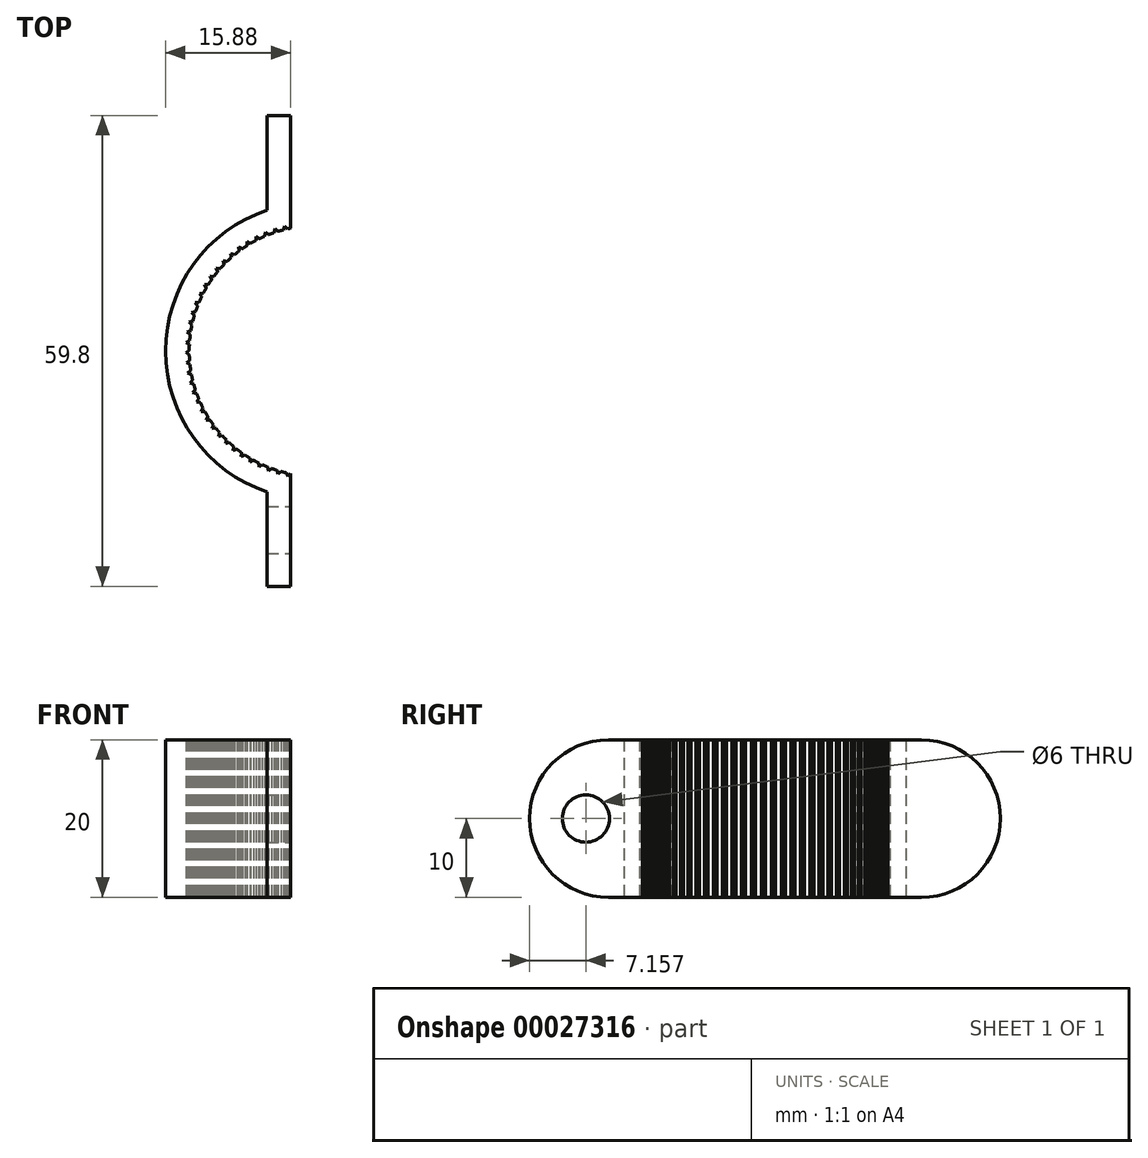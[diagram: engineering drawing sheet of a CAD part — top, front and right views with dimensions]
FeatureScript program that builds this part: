
annotation { "Feature Type Name" : "Feature", "Feature Type Description" : "" }
export const myFeature = defineFeature(function(context is Context, id is Id, definition is map)
    precondition{}
    {
        {
            var Q0;
            Q0=qCreatedBy(makeId("Top.planeOp"),FACE);
            var sketch = newSketch(context, id + "F0", { "sketchPlane" : qUnion([Q0])});
            skLineSegment(sketch, "E0", {"start": v(0, -18.88) * mm, "end": v(0, 18.88) * mm, "construction": true});
            skCircle(sketch, "E1", {"center": v(0, 0) * mm, "radius": 15.88 * mm});
            skCircle(sketch, "E2", {"center": v(0, 0) * mm, "radius": 18.88 * mm});
            skLineSegment(sketch, "E3", {"start": v(-3, 15.59) * mm, "end": v(-3, 29.9) * mm});
            skLineSegment(sketch, "E4", {"start": v(-3, 29.9) * mm, "end": v(-6, 29.9) * mm});
            skLineSegment(sketch, "E5", {"start": v(-6, 29.9) * mm, "end": v(-6, 17.9) * mm});
            skLineSegment(sketch, "E6", {"start": v(-15.88, 0) * mm, "end": v(15.88, 0) * mm, "construction": true});
            skLineSegment(sketch, "E7.MirrorCS", {"start": v(-6, -29.9) * mm, "end": v(-6, -17.9) * mm});
            skLineSegment(sketch, "E8.MirrorCS", {"start": v(-3, -29.9) * mm, "end": v(-6, -29.9) * mm});
            skLineSegment(sketch, "E9.MirrorCS", {"start": v(-3, -15.59) * mm, "end": v(-3, -29.9) * mm});
            skLineSegment(sketch, "E10", {"start": v(-15.88, 0) * mm, "end": v(-18.88, 0) * mm, "construction": true});
            skLineSegment(sketch, "E11", {"start": v(-3, -15.59) * mm, "end": v(-3.34, -15.96) * mm});
            skLineSegment(sketch, "E12", {"start": v(-3.34, -15.96) * mm, "end": v(-3.5, -15.48) * mm});
            skLineSegment(sketch, "E13.1.0", {"start": v(-4.23, -15.3) * mm, "end": v(-4.6, -15.64) * mm});
            skLineSegment(sketch, "E13.1.1", {"start": v(-4.6, -15.64) * mm, "end": v(-4.72, -15.16) * mm});
            skLineSegment(sketch, "E13.2.0", {"start": v(-5.43, -14.92) * mm, "end": v(-5.82, -15.23) * mm});
            skLineSegment(sketch, "E13.2.1", {"start": v(-5.82, -15.23) * mm, "end": v(-5.9, -14.73) * mm});
            skLineSegment(sketch, "E13.3.0", {"start": v(-6.6, -14.44) * mm, "end": v(-7.01, -14.72) * mm});
            skLineSegment(sketch, "E13.3.1", {"start": v(-7.01, -14.72) * mm, "end": v(-7.06, -14.22) * mm});
            skLineSegment(sketch, "E13.4.0", {"start": v(-7.73, -13.87) * mm, "end": v(-8.16, -14.11) * mm});
            skLineSegment(sketch, "E13.4.1", {"start": v(-8.16, -14.11) * mm, "end": v(-8.17, -13.61) * mm});
            skLineSegment(sketch, "E13.5.0", {"start": v(-8.8, -13.21) * mm, "end": v(-9.26, -13.42) * mm});
            skLineSegment(sketch, "E13.5.1", {"start": v(-9.26, -13.42) * mm, "end": v(-9.22, -12.92) * mm});
            skLineSegment(sketch, "E13.6.0", {"start": v(-9.82, -12.47) * mm, "end": v(-10.3, -12.64) * mm});
            skLineSegment(sketch, "E13.6.1", {"start": v(-10.3, -12.64) * mm, "end": v(-10.22, -12.15) * mm});
            skLineSegment(sketch, "E13.7.0", {"start": v(-10.78, -11.65) * mm, "end": v(-11.27, -11.78) * mm});
            skLineSegment(sketch, "E13.7.1", {"start": v(-11.27, -11.78) * mm, "end": v(-11.15, -11.3) * mm});
            skLineSegment(sketch, "E13.8.0", {"start": v(-11.68, -10.76) * mm, "end": v(-12.17, -10.85) * mm});
            skLineSegment(sketch, "E13.8.1", {"start": v(-12.17, -10.85) * mm, "end": v(-12.02, -10.37) * mm});
            skLineSegment(sketch, "E13.9.0", {"start": v(-12.5, -9.8) * mm, "end": v(-13, -9.85) * mm});
            skLineSegment(sketch, "E13.9.1", {"start": v(-13, -9.85) * mm, "end": v(-12.8, -9.39) * mm});
            skLineSegment(sketch, "E13.10.0", {"start": v(-13.23, -8.77) * mm, "end": v(-13.73, -8.79) * mm});
            skLineSegment(sketch, "E13.10.1", {"start": v(-13.73, -8.79) * mm, "end": v(-13.5, -8.34) * mm});
            skLineSegment(sketch, "E13.11.0", {"start": v(-13.89, -7.7) * mm, "end": v(-14.39, -7.67) * mm});
            skLineSegment(sketch, "E13.11.1", {"start": v(-14.39, -7.67) * mm, "end": v(-14.13, -7.24) * mm});
            skLineSegment(sketch, "E13.12.0", {"start": v(-14.45, -6.56) * mm, "end": v(-14.95, -6.5) * mm});
            skLineSegment(sketch, "E13.12.1", {"start": v(-14.95, -6.5) * mm, "end": v(-14.66, -6.1) * mm});
            skLineSegment(sketch, "E13.13.0", {"start": v(-14.93, -5.4) * mm, "end": v(-15.42, -5.3) * mm});
            skLineSegment(sketch, "E13.13.1", {"start": v(-15.42, -5.3) * mm, "end": v(-15.1, -4.91) * mm});
            skLineSegment(sketch, "E13.14.0", {"start": v(-15.31, -4.2) * mm, "end": v(-15.8, -4.05) * mm});
            skLineSegment(sketch, "E13.14.1", {"start": v(-15.8, -4.05) * mm, "end": v(-15.44, -3.7) * mm});
            skLineSegment(sketch, "E13.15.0", {"start": v(-15.6, -2.96) * mm, "end": v(-16.06, -2.78) * mm});
            skLineSegment(sketch, "E13.15.1", {"start": v(-16.06, -2.78) * mm, "end": v(-15.68, -2.46) * mm});
            skLineSegment(sketch, "E13.16.0", {"start": v(-15.78, -1.71) * mm, "end": v(-16.23, -1.5) * mm});
            skLineSegment(sketch, "E13.16.1", {"start": v(-16.23, -1.5) * mm, "end": v(-15.83, -1.2) * mm});
            skLineSegment(sketch, "E13.17.0", {"start": v(-15.87, -0.45) * mm, "end": v(-16.3, -0.2) * mm});
            skLineSegment(sketch, "E13.17.1", {"start": v(-16.3, -0.2) * mm, "end": v(-15.87, 0.06) * mm});
            skLineSegment(sketch, "E13.18.0", {"start": v(-15.85, 0.8) * mm, "end": v(-16.27, 1.1) * mm});
            skLineSegment(sketch, "E13.18.1", {"start": v(-16.27, 1.1) * mm, "end": v(-15.82, 1.32) * mm});
            skLineSegment(sketch, "E13.19.0", {"start": v(-15.74, 2.07) * mm, "end": v(-16.13, 2.38) * mm});
            skLineSegment(sketch, "E13.19.1", {"start": v(-16.13, 2.38) * mm, "end": v(-15.67, 2.57) * mm});
            skLineSegment(sketch, "E13.20.0", {"start": v(-15.53, 3.3) * mm, "end": v(-15.89, 3.65) * mm});
            skLineSegment(sketch, "E13.20.1", {"start": v(-15.89, 3.65) * mm, "end": v(-15.41, 3.8) * mm});
            skLineSegment(sketch, "E13.21.0", {"start": v(-15.21, 4.53) * mm, "end": v(-15.55, 4.9) * mm});
            skLineSegment(sketch, "E13.21.1", {"start": v(-15.55, 4.9) * mm, "end": v(-15.06, 5.02) * mm});
            skLineSegment(sketch, "E13.22.0", {"start": v(-14.8, 5.73) * mm, "end": v(-15.1, 6.13) * mm});
            skLineSegment(sketch, "E13.22.1", {"start": v(-15.1, 6.13) * mm, "end": v(-14.61, 6.2) * mm});
            skLineSegment(sketch, "E13.23.0", {"start": v(-14.3, 6.89) * mm, "end": v(-14.57, 7.3) * mm});
            skLineSegment(sketch, "E13.23.1", {"start": v(-14.57, 7.3) * mm, "end": v(-14.08, 7.34) * mm});
            skLineSegment(sketch, "E13.24.0", {"start": v(-13.71, 8) * mm, "end": v(-13.95, 8.44) * mm});
            skLineSegment(sketch, "E13.24.1", {"start": v(-13.95, 8.44) * mm, "end": v(-13.45, 8.44) * mm});
            skLineSegment(sketch, "E13.25.0", {"start": v(-13.03, 9.06) * mm, "end": v(-13.23, 9.52) * mm});
            skLineSegment(sketch, "E13.25.1", {"start": v(-13.23, 9.52) * mm, "end": v(-12.73, 9.48) * mm});
            skLineSegment(sketch, "E13.26.0", {"start": v(-12.27, 10.07) * mm, "end": v(-12.43, 10.54) * mm});
            skLineSegment(sketch, "E13.26.1", {"start": v(-12.43, 10.54) * mm, "end": v(-11.94, 10.46) * mm});
            skLineSegment(sketch, "E13.27.0", {"start": v(-11.43, 11.01) * mm, "end": v(-11.56, 11.5) * mm});
            skLineSegment(sketch, "E13.27.1", {"start": v(-11.56, 11.5) * mm, "end": v(-11.07, 11.38) * mm});
            skLineSegment(sketch, "E13.28.0", {"start": v(-10.52, 11.89) * mm, "end": v(-10.6, 12.38) * mm});
            skLineSegment(sketch, "E13.28.1", {"start": v(-10.6, 12.38) * mm, "end": v(-10.13, 12.22) * mm});
            skLineSegment(sketch, "E13.29.0", {"start": v(-9.54, 12.69) * mm, "end": v(-9.6, 13.18) * mm});
            skLineSegment(sketch, "E13.29.1", {"start": v(-9.6, 13.18) * mm, "end": v(-9.13, 12.99) * mm});
            skLineSegment(sketch, "E13.30.0", {"start": v(-8.5, 13.4) * mm, "end": v(-8.51, 13.9) * mm});
            skLineSegment(sketch, "E13.30.1", {"start": v(-8.51, 13.9) * mm, "end": v(-8.07, 13.67) * mm});
            skLineSegment(sketch, "E13.31.0", {"start": v(-7.41, 14.04) * mm, "end": v(-7.38, 14.54) * mm});
            skLineSegment(sketch, "E13.31.1", {"start": v(-7.38, 14.54) * mm, "end": v(-6.96, 14.27) * mm});
            skLineSegment(sketch, "E13.32.0", {"start": v(-6.28, 14.58) * mm, "end": v(-6.2, 15.08) * mm});
            skLineSegment(sketch, "E13.32.1", {"start": v(-6.2, 15.08) * mm, "end": v(-5.8, 14.78) * mm});
            skLineSegment(sketch, "E13.33.0", {"start": v(-5.1, 15.03) * mm, "end": v(-4.99, 15.52) * mm});
            skLineSegment(sketch, "E13.33.1", {"start": v(-4.99, 15.52) * mm, "end": v(-4.61, 15.2) * mm});
            skLineSegment(sketch, "E13.34.0", {"start": v(-3.89, 15.4) * mm, "end": v(-3.74, 15.87) * mm});
            skLineSegment(sketch, "E13.34.1", {"start": v(-3.74, 15.87) * mm, "end": v(-3.39, 15.5) * mm});
            skLineSegment(sketch, "E13.35.0", {"start": v(-2.65, 15.65) * mm, "end": v(-2.46, 16.12) * mm});
            skLineSegment(sketch, "E13.35.1", {"start": v(-2.46, 16.12) * mm, "end": v(-2.15, 15.73) * mm});
            skLineSegment(sketch, "E13.36.0", {"start": v(-1.4, 15.81) * mm, "end": v(-1.18, 16.26) * mm});
            skLineSegment(sketch, "E13.36.1", {"start": v(-1.18, 16.26) * mm, "end": v(-0.89, 15.85) * mm});
            skLineSegment(sketch, "E13.37.0", {"start": v(-0.14, 15.87) * mm, "end": v(0.12, 16.3) * mm});
            skLineSegment(sketch, "E13.37.1", {"start": v(0.12, 16.3) * mm, "end": v(0.37, 15.87) * mm});
            skLineSegment(sketch, "E13.38.0", {"start": v(1.12, 15.84) * mm, "end": v(1.42, 16.24) * mm});
            skLineSegment(sketch, "E13.38.1", {"start": v(1.42, 16.24) * mm, "end": v(1.63, 15.8) * mm});
            skLineSegment(sketch, "E13.39.0", {"start": v(2.38, 15.7) * mm, "end": v(2.7, 16.08) * mm});
            skLineSegment(sketch, "E13.39.1", {"start": v(2.7, 16.08) * mm, "end": v(2.88, 15.61) * mm});
            skLineSegment(sketch, "E13.anchor1", {"start": v(0, 0) * mm, "end": v(-3.34, -15.96) * mm, "construction": true});
            skLineSegment(sketch, "E13.anchor2", {"start": v(0, 0) * mm, "end": v(-3.34, -15.96) * mm, "construction": true});
            skLineSegment(sketch, "E14.2.40.0", {"start": v(3.62, 15.46) * mm, "end": v(3.97, 15.81) * mm});
            skLineSegment(sketch, "E14.3.40.0", {"start": v(3.97, 15.81) * mm, "end": v(4.11, 15.33) * mm});
            skLineSegment(sketch, "E14.2.41.0", {"start": v(4.83, 15.12) * mm, "end": v(5.21, 15.45) * mm});
            skLineSegment(sketch, "E14.3.41.0", {"start": v(5.21, 15.45) * mm, "end": v(5.32, 14.96) * mm});
            skLineSegment(sketch, "E14.2.42.0", {"start": v(6.02, 14.69) * mm, "end": v(6.42, 14.98) * mm});
            skLineSegment(sketch, "E14.3.42.0", {"start": v(6.42, 14.98) * mm, "end": v(6.49, 14.49) * mm});
            skLineSegment(sketch, "E14.2.43.0", {"start": v(7.17, 14.16) * mm, "end": v(7.6, 14.43) * mm});
            skLineSegment(sketch, "E14.3.43.0", {"start": v(7.6, 14.43) * mm, "end": v(7.62, 13.93) * mm});
            skLineSegment(sketch, "E14.2.44.0", {"start": v(8.27, 13.55) * mm, "end": v(8.72, 13.78) * mm});
            skLineSegment(sketch, "E14.3.44.0", {"start": v(8.72, 13.78) * mm, "end": v(8.7, 13.28) * mm});
            skLineSegment(sketch, "E14.2.45.0", {"start": v(9.32, 12.85) * mm, "end": v(9.78, 13.04) * mm});
            skLineSegment(sketch, "E14.3.45.0", {"start": v(9.78, 13.04) * mm, "end": v(9.73, 12.54) * mm});
            skLineSegment(sketch, "E14.2.46.0", {"start": v(10.31, 12.07) * mm, "end": v(10.79, 12.22) * mm});
            skLineSegment(sketch, "E14.3.46.0", {"start": v(10.79, 12.22) * mm, "end": v(10.7, 11.73) * mm});
            skLineSegment(sketch, "E14.2.47.0", {"start": v(11.24, 11.21) * mm, "end": v(11.73, 11.33) * mm});
            skLineSegment(sketch, "E14.3.47.0", {"start": v(11.73, 11.33) * mm, "end": v(11.6, 10.84) * mm});
            skLineSegment(sketch, "E14.2.48.0", {"start": v(12.1, 10.28) * mm, "end": v(12.59, 10.36) * mm});
            skLineSegment(sketch, "E14.3.48.0", {"start": v(12.59, 10.36) * mm, "end": v(12.42, 9.89) * mm});
            skLineSegment(sketch, "E14.2.49.0", {"start": v(12.87, 9.29) * mm, "end": v(13.37, 9.33) * mm});
            skLineSegment(sketch, "E14.3.49.0", {"start": v(13.37, 9.33) * mm, "end": v(13.17, 8.87) * mm});
            skLineSegment(sketch, "E14.2.50.0", {"start": v(13.57, 8.24) * mm, "end": v(14.07, 8.23) * mm});
            skLineSegment(sketch, "E14.3.50.0", {"start": v(14.07, 8.23) * mm, "end": v(13.83, 7.8) * mm});
            skLineSegment(sketch, "E14.2.51.0", {"start": v(14.18, 7.13) * mm, "end": v(14.68, 7.1) * mm});
            skLineSegment(sketch, "E14.3.51.0", {"start": v(14.68, 7.1) * mm, "end": v(14.4, 6.67) * mm});
            skLineSegment(sketch, "E14.2.52.0", {"start": v(14.7, 5.98) * mm, "end": v(15.2, 5.9) * mm});
            skLineSegment(sketch, "E14.3.52.0", {"start": v(15.2, 5.9) * mm, "end": v(14.89, 5.5) * mm});
            skLineSegment(sketch, "E14.2.53.0", {"start": v(15.13, 4.8) * mm, "end": v(15.62, 4.68) * mm});
            skLineSegment(sketch, "E14.3.53.0", {"start": v(15.62, 4.68) * mm, "end": v(15.28, 4.3) * mm});
            skLineSegment(sketch, "E14.2.54.0", {"start": v(15.47, 3.58) * mm, "end": v(15.94, 3.42) * mm});
            skLineSegment(sketch, "E14.3.54.0", {"start": v(15.94, 3.42) * mm, "end": v(15.57, 3.08) * mm});
            skLineSegment(sketch, "E14.2.55.0", {"start": v(15.7, 2.34) * mm, "end": v(16.16, 2.14) * mm});
            skLineSegment(sketch, "E14.3.55.0", {"start": v(16.16, 2.14) * mm, "end": v(15.77, 1.83) * mm});
            skLineSegment(sketch, "E14.2.56.0", {"start": v(15.84, 1.08) * mm, "end": v(16.28, 0.85) * mm});
            skLineSegment(sketch, "E14.3.56.0", {"start": v(16.28, 0.85) * mm, "end": v(15.86, 0.57) * mm});
            skLineSegment(sketch, "E14.2.57.0", {"start": v(15.87, -0.18) * mm, "end": v(16.3, -0.44) * mm});
            skLineSegment(sketch, "E14.3.57.0", {"start": v(16.3, -0.44) * mm, "end": v(15.86, -0.69) * mm});
            skLineSegment(sketch, "E14.2.58.0", {"start": v(15.8, -1.44) * mm, "end": v(16.2, -1.74) * mm});
            skLineSegment(sketch, "E14.3.58.0", {"start": v(16.2, -1.74) * mm, "end": v(15.76, -1.95) * mm});
            skLineSegment(sketch, "E14.2.59.0", {"start": v(15.65, -2.69) * mm, "end": v(16.02, -3.02) * mm});
            skLineSegment(sketch, "E14.3.59.0", {"start": v(16.02, -3.02) * mm, "end": v(15.55, -3.2) * mm});
            skLineSegment(sketch, "E14.2.60.0", {"start": v(15.38, -3.92) * mm, "end": v(15.73, -4.28) * mm});
            skLineSegment(sketch, "E14.3.60.0", {"start": v(15.73, -4.28) * mm, "end": v(15.25, -4.42) * mm});
            skLineSegment(sketch, "E14.2.61.0", {"start": v(15.02, -5.13) * mm, "end": v(15.34, -5.52) * mm});
            skLineSegment(sketch, "E14.3.61.0", {"start": v(15.34, -5.52) * mm, "end": v(14.85, -5.61) * mm});
            skLineSegment(sketch, "E14.2.62.0", {"start": v(14.57, -6.31) * mm, "end": v(14.85, -6.72) * mm});
            skLineSegment(sketch, "E14.3.62.0", {"start": v(14.85, -6.72) * mm, "end": v(14.36, -6.78) * mm});
            skLineSegment(sketch, "E14.2.63.0", {"start": v(14.02, -7.45) * mm, "end": v(14.27, -7.88) * mm});
            skLineSegment(sketch, "E14.3.63.0", {"start": v(14.27, -7.88) * mm, "end": v(13.77, -7.9) * mm});
            skLineSegment(sketch, "E14.2.64.0", {"start": v(13.38, -8.54) * mm, "end": v(13.6, -8.99) * mm});
            skLineSegment(sketch, "E14.3.64.0", {"start": v(13.6, -8.99) * mm, "end": v(13.1, -8.96) * mm});
            skLineSegment(sketch, "E14.2.65.0", {"start": v(12.66, -9.57) * mm, "end": v(12.84, -10.04) * mm});
            skLineSegment(sketch, "E14.3.65.0", {"start": v(12.84, -10.04) * mm, "end": v(12.35, -9.98) * mm});
            skLineSegment(sketch, "E14.2.66.0", {"start": v(11.86, -10.55) * mm, "end": v(12, -11.03) * mm});
            skLineSegment(sketch, "E14.3.66.0", {"start": v(12, -11.03) * mm, "end": v(11.52, -10.93) * mm});
            skLineSegment(sketch, "E14.2.67.0", {"start": v(10.99, -11.46) * mm, "end": v(11.1, -11.95) * mm});
            skLineSegment(sketch, "E14.3.67.0", {"start": v(11.1, -11.95) * mm, "end": v(10.61, -11.8) * mm});
            skLineSegment(sketch, "E14.2.68.0", {"start": v(10.04, -12.3) * mm, "end": v(10.1, -12.8) * mm});
            skLineSegment(sketch, "E14.3.68.0", {"start": v(10.1, -12.8) * mm, "end": v(9.64, -12.61) * mm});
            skLineSegment(sketch, "E14.2.69.0", {"start": v(9.03, -13.06) * mm, "end": v(9.06, -13.55) * mm});
            skLineSegment(sketch, "E14.3.69.0", {"start": v(9.06, -13.55) * mm, "end": v(8.6, -13.34) * mm});
            skLineSegment(sketch, "E14.2.70.0", {"start": v(7.97, -13.73) * mm, "end": v(7.95, -14.23) * mm});
            skLineSegment(sketch, "E14.3.70.0", {"start": v(7.95, -14.23) * mm, "end": v(7.52, -13.98) * mm});
            skLineSegment(sketch, "E14.2.71.0", {"start": v(6.85, -14.32) * mm, "end": v(6.8, -14.82) * mm});
            skLineSegment(sketch, "E14.3.71.0", {"start": v(6.8, -14.82) * mm, "end": v(6.39, -14.53) * mm});
            skLineSegment(sketch, "E14.2.72.0", {"start": v(5.7, -14.82) * mm, "end": v(5.6, -15.31) * mm});
            skLineSegment(sketch, "E14.3.72.0", {"start": v(5.6, -15.31) * mm, "end": v(5.21, -15) * mm});
            skLineSegment(sketch, "E14.2.73.0", {"start": v(4.5, -15.23) * mm, "end": v(4.36, -15.7) * mm});
            skLineSegment(sketch, "E14.3.73.0", {"start": v(4.36, -15.7) * mm, "end": v(4, -15.36) * mm});
            skLineSegment(sketch, "E14.2.74.0", {"start": v(3.27, -15.53) * mm, "end": v(3.1, -16) * mm});
            skLineSegment(sketch, "E14.3.74.0", {"start": v(3.1, -16) * mm, "end": v(2.77, -15.63) * mm});
            skLineSegment(sketch, "E14.2.75.0", {"start": v(2.03, -15.75) * mm, "end": v(1.82, -16.2) * mm});
            skLineSegment(sketch, "E14.3.75.0", {"start": v(1.82, -16.2) * mm, "end": v(1.52, -15.8) * mm});
            skLineSegment(sketch, "E14.2.76.0", {"start": v(0.77, -15.86) * mm, "end": v(0.53, -16.3) * mm});
            skLineSegment(sketch, "E14.3.76.0", {"start": v(0.53, -16.3) * mm, "end": v(0.26, -15.87) * mm});
            skLineSegment(sketch, "E14.2.77.0", {"start": v(-0.5, -15.87) * mm, "end": v(-0.77, -16.28) * mm});
            skLineSegment(sketch, "E14.3.77.0", {"start": v(-0.77, -16.28) * mm, "end": v(-1, -15.84) * mm});
            skLineSegment(sketch, "E14.2.78.0", {"start": v(-1.75, -15.78) * mm, "end": v(-2.06, -16.17) * mm});
            skLineSegment(sketch, "E14.3.78.0", {"start": v(-2.06, -16.17) * mm, "end": v(-2.26, -15.71) * mm});
            skSolve(sketch);
        }
        {
            var Q0;
            {var subQ0=sQuery(id+"F0.wireOp",EDGE,"E3");var subQ3=sQuery(id+"F0.wireOp",EDGE,"E1");var subQ4=makeQuery(id+"F0.imprint","INTERSECT",VERTEX,{"derivedFrom":[subQ3,subQ0]});Q0=makeQuery(id+"F0.imprint","IMPRINT",FACE,{"disambiguationData":[TD([[makeQuery(id+"F0.imprint","IMPRINT",EDGE,{"disambiguationData":[TD([[subQ4,-1.0]])],"derivedFrom":subQ3}),-1.0]])]});}
            var Q1;
            {var subQ4=sQuery(id+"F0.wireOp",EDGE,"E7.MirrorCS");Q1=makeQuery(id+"F0.imprint","IMPRINT",FACE,{"disambiguationData":[TD([[makeQuery(id+"F0.imprint","IMPRINT",EDGE,{"derivedFrom":subQ4}),-1.0]])]});}
            var Q2;
            {var subQ1=sQuery(id+"F0.wireOp",EDGE,"E4");Q2=makeQuery(id+"F0.imprint","IMPRINT",FACE,{"disambiguationData":[TD([[makeQuery(id+"F0.imprint","IMPRINT",EDGE,{"derivedFrom":subQ1}),1.0]])]});}
            var Q3;
            {var subQ19=sQuery(id+"F0.wireOp",EDGE,"E11");Q3=makeQuery(id+"F0.imprint","IMPRINT",FACE,{"disambiguationData":[TD([[makeQuery(id+"F0.imprint","IMPRINT",EDGE,{"derivedFrom":subQ19}),1.0]])]});}
            extrude(context, id + "F1", {"entities" : qUnion([Q0, Q1, Q2, Q3]), "depth" : 20 * mm});
        }
        {
            var Q0;
            Q0=makeQuery(id+"F1.opExtrude","SWEPT_FACE",FACE,{"disambiguationData":[OSD([sQuery(id+"F0.wireOp",EDGE,"E9.MirrorCS")])]});
            var sketch = newSketch(context, id + "F2", { "sketchPlane" : qUnion([Q0])});
            skLineSegment(sketch, "E15.0", {"start": v(-15.59, 20) * mm, "end": v(-29.9, 20) * mm});
            skLineSegment(sketch, "E15.1", {"start": v(-29.9, 20) * mm, "end": v(-29.9, 0) * mm});
            skLineSegment(sketch, "E15.2", {"start": v(-15.59, 20) * mm, "end": v(-15.59, 0) * mm});
            skLineSegment(sketch, "E15.3", {"start": v(-15.59, 0) * mm, "end": v(-29.9, 0) * mm});
            skLineSegment(sketch, "E16", {"start": v(0, 0) * mm, "end": v(0, 20.29) * mm, "construction": true});
            skCircle(sketch, "E17", {"center": v(-22.74, 10) * mm, "radius": 3 * mm});
            skCircle(sketch, "E18.MirrorC", {"center": v(22.74, 10) * mm, "radius": 3 * mm});
            skSolve(sketch);
        }
        {
            var Q0;
            Q0=makeQuery(id+"F2.imprint","IMPRINT",FACE,{"disambiguationData":[TD([[makeQuery(id+"F2.imprint","IMPRINT",EDGE,{"derivedFrom":sQuery(id+"F2.wireOp",EDGE,"E17")}),1.0]])]});
            var Q1;
            Q1=makeQuery(id+"F2.imprint","IMPRINT",FACE,{"disambiguationData":[TD([[makeQuery(id+"F2.imprint","IMPRINT",EDGE,{"derivedFrom":sQuery(id+"F2.wireOp",EDGE,"E18.MirrorC")}),-1.0]])]});
            extrude(context, id + "F3", {"entities" : qUnion([Q0, Q1]), "operationType" : NewBodyOperationType.REMOVE, "endBound" : BoundingType.THROUGH_ALL, "oppositeDirection" : true, "depth" : 25 * mm});
        }
        {
            var Q0;
            Q0=makeQuery(id+"F1.opExtrude","CAP_EDGE",EDGE,{"disambiguationData":[OSD([sQuery(id+"F0.wireOp",EDGE,"E8.MirrorCS")])],"isStart":false});
            var Q1;
            Q1=makeQuery(id+"F1.opExtrude","CAP_EDGE",EDGE,{"disambiguationData":[OSD([sQuery(id+"F0.wireOp",EDGE,"E8.MirrorCS")])],"isStart":true});
            var Q2;
            Q2=makeQuery(id+"F1.opExtrude","CAP_EDGE",EDGE,{"disambiguationData":[OSD([sQuery(id+"F0.wireOp",EDGE,"E4")])],"isStart":true});
            var Q3;
            Q3=makeQuery(id+"F1.opExtrude","CAP_EDGE",EDGE,{"disambiguationData":[OSD([sQuery(id+"F0.wireOp",EDGE,"E4")])],"isStart":false});
            fillet(context, id + "F4", {"entities" : qUnion([Q0, Q1, Q2, Q3]), "radius" : 10 * mm, "tangentPropagation" : true, "allowEdgeOverflow" : false});
        }
    });
